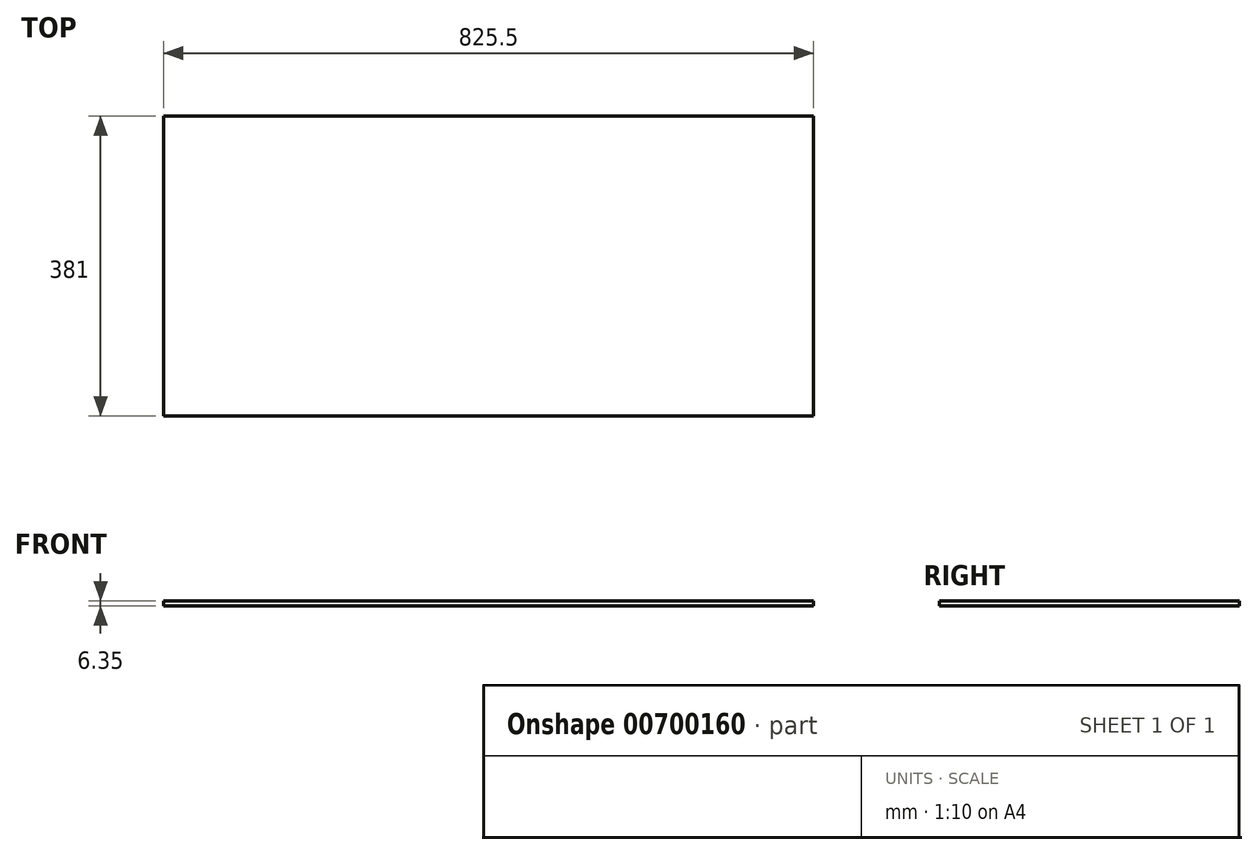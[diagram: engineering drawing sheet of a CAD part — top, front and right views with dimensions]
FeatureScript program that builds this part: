
annotation { "Feature Type Name" : "Feature", "Feature Type Description" : "" }
export const myFeature = defineFeature(function(context is Context, id is Id, definition is map)
    precondition{}
    {
        {
            var Q0;
            Q0=qCreatedBy(makeId("Top.planeOp"),FACE);
            var sketch = newSketch(context, id + "F0", { "sketchPlane" : qUnion([Q0])});
            skLineSegment(sketch, "E0.bottom", {"start": v(412.75, 190.5) * mm, "end": v(-412.75, 190.5) * mm});
            skLineSegment(sketch, "E0.top", {"start": v(412.75, -190.5) * mm, "end": v(-412.75, -190.5) * mm});
            skLineSegment(sketch, "E0.left", {"start": v(412.75, 190.5) * mm, "end": v(412.75, -190.5) * mm});
            skLineSegment(sketch, "E0.right", {"start": v(-412.75, 190.5) * mm, "end": v(-412.75, -190.5) * mm});
            skPoint(sketch, "E0.middle", {"position": v(0, 0) * mm});
            skSolve(sketch);
        }
        {
            var Q0;
            Q0=makeQuery(id+"F0.imprint","IMPRINT",FACE,{"disambiguationData":[TD([[makeQuery(id+"F0.imprint","IMPRINT",EDGE,{"derivedFrom":sQuery(id+"F0.wireOp",EDGE,"E0.bottom")}),1.0]])]});
            extrude(context, id + "F1", {"entities" : qUnion([Q0]), "depth" : 6.35 * mm, "offsetDistance" : 25.4 * mm});
        }
    });
